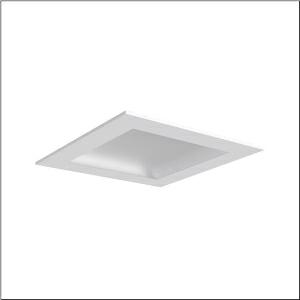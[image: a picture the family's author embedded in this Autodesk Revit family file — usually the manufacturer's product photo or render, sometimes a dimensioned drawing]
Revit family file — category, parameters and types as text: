
# Revit family: mira_11_sl_51fr427a453a
name_source: partatom
category: Lighting Fixtures
units: mm (PartAtom-declared; Revit-internal decimal feet)

## family parameters
Cut with Voids When Loaded = No
Host = Face
Light Source = No
Part Type = Normal
Room Calculation Point = No
Round Connector Dimension = Use Diameter
Shared = No

## types (1)
- Mira 11 SL (1 x LED, 5850 lm, 58 W, 4000K)
    Apparent Load = 58 VA
    CIE Flux Codes = 50 81 97 100 100
    Color Rendering = 80
    Color Temperature = 4000K
    Default Elevation = 1800 mm
    Description = Mira 11 SL, clean room luminaire, primary light control with reflector, primary optical cover: cover, of PC, light emission: direct distribution, primary light characteristic: symmetric, installation type: recessed, LED, rated luminous flux: 5.850lm, luminous efficacy: 101lm/W, light colour: 840, colour temperature: 4000K, control gear: ON/OFF, with terminal, 3-pole, max. 2.5mm², mains connection: 230V, AC, 50/60Hz, rated input power: 58W, luminaire housing, of sheet steel, coated, pure white (RAL 9010), with wing nuts, module: M625, length: 623mm, width: 623mm, height: 91mm, protection rating (complete): IP54, protection rating (on room side): IP65, insulation class (complete): insulation class I (protective earthing), certification: CE, UKCA, permissible operating ambient temperature: -5..+40°C, standard: EN 50419, packaging unit: 1 piece
    Height = 0 mm  [stored 0 ft]
    Lamp = 1 x LED
    Lamp Light Flux = 5850 lm
    Lamp Power = 58 W
    Lamp count = 1
    Length = 625 mm
    Luminous efficacy = 101 lm/W
    Manufacturer = Siteco
    ModVariant = No
    Model = 51FR427A453A
    Mounting Place = Ceiling
    Mounting Type = Recessed
    Number of Poles = 1
    OnlyDefault = Yes
    Power Factor = 1
    Product Name = Mira 11 SL
    Product group = clean room luminaire | ceiling recessed
    ProductGroupID = 402
    Protection Class = Protection class I
    Protection Degree = IP 54
    RLX_Detail_Level = 1
    RLX_Emergency_Light_Flux = 0 lm
    RLX_Emergency_Type = 0
    RLX_Emergency_Type_DB = No
    RlxData = <blob elided: 19913 chars, md5=97d21306>
    Socket = socket
    Standby Power = 0 W
    System Light Flux = 5850 lm
    System Power = 58 W
    Type Comments = Product without accessories
    Type Image = l_1007111.jpg
    URL = http://relux.com
    VarID = ---
    Voltage = 0 V
    Weight = 0.00 kg
    Width = 625 mm

note: [stored X ft] marks values corroborated as IEEE doubles in the binary element streams (Revit-internal decimal feet)

## geometry (parser evidence)
native form markers: Blend x4, Sweep x10
no freeform markers — native parametric forms only
